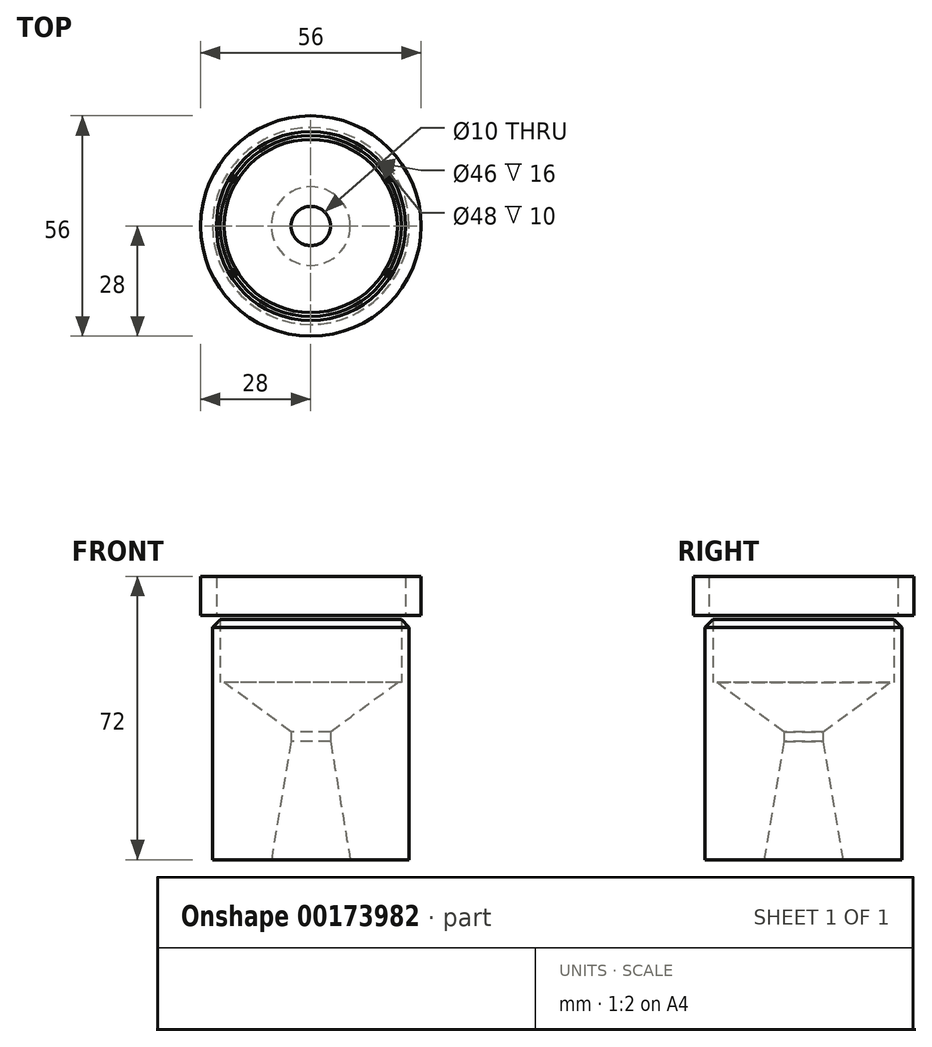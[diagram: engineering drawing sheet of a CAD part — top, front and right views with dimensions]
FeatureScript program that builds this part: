
annotation { "Feature Type Name" : "Feature", "Feature Type Description" : "" }
export const myFeature = defineFeature(function(context is Context, id is Id, definition is map)
    precondition{}
    {
        {
            var Q0;
            Q0=qCreatedBy(makeId("Top.planeOp"),FACE);
            var sketch = newSketch(context, id + "F0", { "sketchPlane" : qUnion([Q0])});
            skCircle(sketch, "E0", {"center": v(0, 0) * mm, "radius": 5 * mm});
            skCircle(sketch, "E1", {"center": v(0, 0) * mm, "radius": 25 * mm});
            skSolve(sketch);
        }
        {
            var Q0;
            Q0=makeQuery(id+"F0.imprint","IMPRINT",FACE,{"disambiguationData":[TD([[makeQuery(id+"F0.imprint","IMPRINT",EDGE,{"derivedFrom":sQuery(id+"F0.wireOp",EDGE,"E0")}),-1.0]])]});
            extrude(context, id + "F1", {"entities" : qUnion([Q0]), "depth" : 45 * mm});
        }
        {
            var Q0;
            Q0=makeQuery(id+"F1.opExtrude","CAP_EDGE",EDGE,{"disambiguationData":[OSD([sQuery(id+"F0.wireOp",EDGE,"E0")])],"isStart":false});
            chamfer(context, id + "F2", {"entities" : qUnion([Q0]), "chamferType" : ChamferType.TWO_OFFSETS, "width1" : 12.5 * mm, "oppositeDirection" : false, "width2" : 17 * mm, "tangentPropagation" : true});
        }
        {
            var Q0;
            Q0=makeQuery(id+"F1.opExtrude","CAP_FACE",FACE,{"disambiguationData":[OSD([sQuery(id+"F0.wireOp",EDGE,"E0"),sQuery(id+"F0.wireOp",EDGE,"E1")])],"isStart":false});
            var sketch = newSketch(context, id + "F3", { "sketchPlane" : qUnion([Q0])});
            skCircle(sketch, "E2", {"center": v(0, 0) * mm, "radius": 23 * mm});
            skCircle(sketch, "E3", {"center": v(0, 0) * mm, "radius": 25 * mm});
            skSolve(sketch);
        }
        {
            var Q0;
            Q0=makeQuery(id+"F3.imprint","IMPRINT",FACE,{"disambiguationData":[TD([[makeQuery(id+"F3.imprint","IMPRINT",EDGE,{"derivedFrom":sQuery(id+"F3.wireOp",EDGE,"E2")}),-1.0]])]});
            extrude(context, id + "F4", {"entities" : qUnion([Q0]), "operationType" : NewBodyOperationType.ADD, "depth" : 17 * mm});
        }
        {
            var Q0;
            Q0=makeQuery(id+"F4.opExtrude","CAP_FACE",FACE,{"disambiguationData":[OSD([sQuery(id+"F3.wireOp",EDGE,"E2"),sQuery(id+"F3.wireOp",EDGE,"E3")])],"isStart":false});
            var sketch = newSketch(context, id + "F5", { "sketchPlane" : qUnion([Q0])});
            skCircle(sketch, "E4", {"center": v(0, 0) * mm, "radius": 28 * mm});
            skCircle(sketch, "E5", {"center": v(0, 0) * mm, "radius": 24 * mm});
            skSolve(sketch);
        }
        {
            var Q0;
            Q0=makeQuery(id+"F5.imprint","IMPRINT",FACE,{"disambiguationData":[TD([[makeQuery(id+"F5.imprint","IMPRINT",EDGE,{"derivedFrom":sQuery(id+"F5.wireOp",EDGE,"E4")}),1.0]])]});
            var Q1;
            Q1=makeQuery(id+"F5.imprint","IMPRINT",FACE,{"disambiguationData":[TD([[makeQuery(id+"F5.imprint","IMPRINT",EDGE,{"derivedFrom":sQuery(id+"F5.wireOp",EDGE,"E5")}),-1.0]])]});
            extrude(context, id + "F6", {"entities" : qUnion([Q0, Q1]), "depth" : 10 * mm});
        }
        {
            var Q0;
            Q0=makeQuery(id+"F4.opExtrude","CAP_EDGE",EDGE,{"disambiguationData":[OSD([sQuery(id+"F3.wireOp",EDGE,"E3")])],"isStart":false});
            chamfer(context, id + "F7", {"entities" : qUnion([Q0]), "width" : 3 * mm, "tangentPropagation" : true});
        }
        {
            var Q0;
            Q0=makeQuery(id+"F1.opExtrude","CAP_EDGE",EDGE,{"disambiguationData":[OSD([sQuery(id+"F0.wireOp",EDGE,"E0")])],"isStart":true});
            chamfer(context, id + "F8", {"entities" : qUnion([Q0]), "chamferType" : ChamferType.TWO_OFFSETS, "width1" : 5 * mm, "oppositeDirection" : false, "width2" : 30 * mm, "tangentPropagation" : true});
        }
    });
